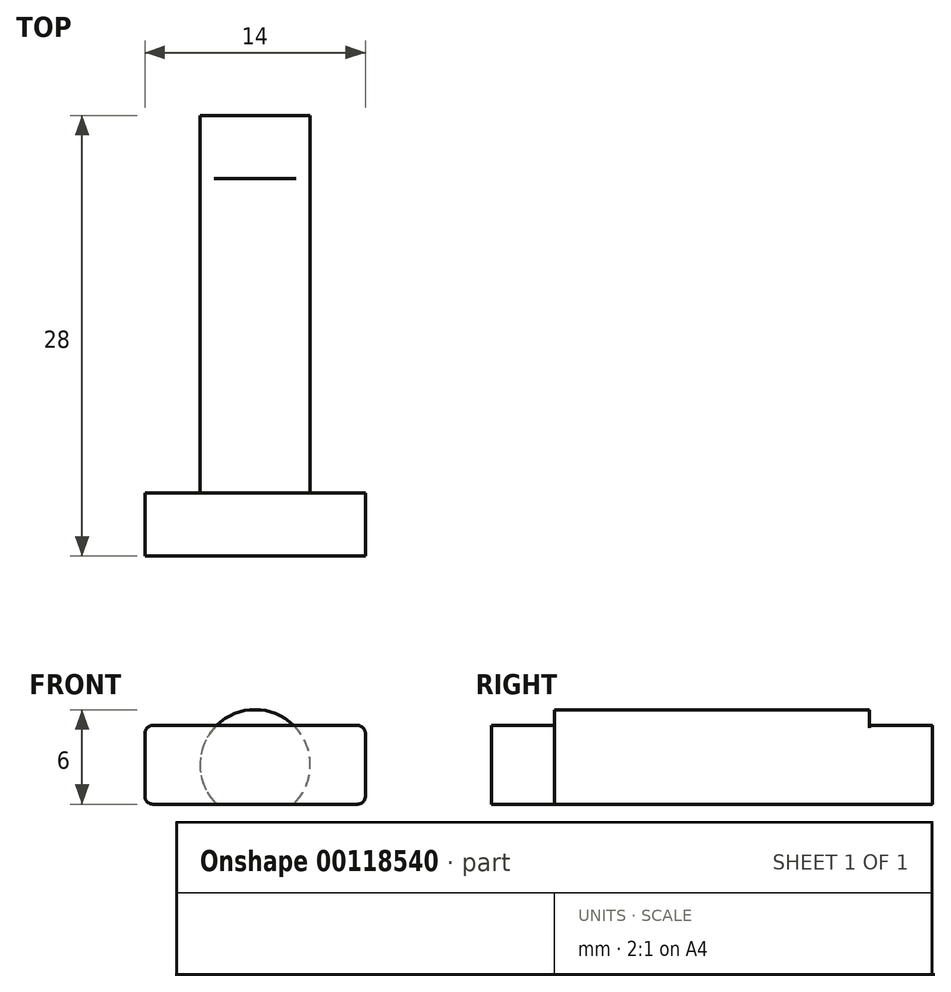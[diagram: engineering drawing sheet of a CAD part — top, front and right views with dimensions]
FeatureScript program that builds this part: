
annotation { "Feature Type Name" : "Feature", "Feature Type Description" : "" }
export const myFeature = defineFeature(function(context is Context, id is Id, definition is map)
    precondition{}
    {
        {
            var Q0;
            Q0=qCreatedBy(makeId("Front.planeOp"),FACE);
            var sketch = newSketch(context, id + "F0", { "sketchPlane" : qUnion([Q0])});
            skArc(sketch, "E0", {"start": v(2.45, 0) * mm, "mid": v(0, 6) * mm, "end": v(-2.45, 0) * mm});
            skLineSegment(sketch, "E1", {"start": v(-2.45, 0) * mm, "end": v(2.45, 0) * mm});
            skSolve(sketch);
        }
        {
            var Q0;
            Q0=makeQuery(id+"F0.imprint","IMPRINT",FACE,{"disambiguationData":[TD([[makeQuery(id+"F0.imprint","IMPRINT",EDGE,{"derivedFrom":sQuery(id+"F0.wireOp",EDGE,"E0")}),1.0]])]});
            extrude(context, id + "F1", {"entities" : qUnion([Q0]), "endBound" : BoundingType.SYMMETRIC, "depth" : 20 * mm});
        }
        {
            var Q0;
            Q0=makeQuery(id+"F1.opExtrude","CAP_FACE",FACE,{"disambiguationData":[OSD([sQuery(id+"F0.wireOp",EDGE,"E0"),sQuery(id+"F0.wireOp",EDGE,"E1")])],"isStart":false});
            var sketch = newSketch(context, id + "F2", { "sketchPlane" : qUnion([Q0])});
            skCircle(sketch, "E2", {"center": v(0, 2.5) * mm, "radius": 3.5 * mm, "construction": true});
            skLineSegment(sketch, "E3.bottom", {"start": v(-7, 5) * mm, "end": v(7, 5) * mm});
            skLineSegment(sketch, "E3.top", {"start": v(-7, 0) * mm, "end": v(7, 0) * mm});
            skLineSegment(sketch, "E3.left", {"start": v(-7, 5) * mm, "end": v(-7, 0) * mm});
            skLineSegment(sketch, "E3.right", {"start": v(7, 5) * mm, "end": v(7, 0) * mm});
            skSolve(sketch);
        }
        {
            var Q0;
            Q0=makeQuery(id+"F2.imprint","IMPRINT",FACE,{"disambiguationData":[TD([[makeQuery(id+"F2.imprint","IMPRINT",EDGE,{"derivedFrom":sQuery(id+"F2.wireOp",EDGE,"E3.bottom")}),-1.0]])]});
            extrude(context, id + "F3", {"entities" : qUnion([Q0]), "operationType" : NewBodyOperationType.ADD, "depth" : 4 * mm});
        }
        {
            var Q0;
            Q0=makeQuery(id+"F1.opExtrude","CAP_FACE",FACE,{"disambiguationData":[OSD([sQuery(id+"F0.wireOp",EDGE,"E0"),sQuery(id+"F0.wireOp",EDGE,"E1")])],"isStart":true});
            var sketch = newSketch(context, id + "F4", { "sketchPlane" : qUnion([Q0])});
            skCircle(sketch, "E4", {"center": v(0, 2.5) * mm, "radius": 3.5 * mm, "construction": true});
            skLineSegment(sketch, "E5.bottom", {"start": v(-2.45, 0) * mm, "end": v(2.45, 0) * mm});
            skLineSegment(sketch, "E5.top", {"start": v(-2.45, 5) * mm, "end": v(2.45, 5) * mm});
            skSolve(sketch);
        }
        {
            var Q0;
            Q0=makeQuery(id+"F4.imprint","IMPRINT",FACE,{"disambiguationData":[TD([[makeQuery(id+"F4.imprint","IMPRINT",EDGE,{"derivedFrom":sQuery(id+"F4.wireOp",EDGE,"E5.bottom")}),-1.0]])]});
            extrude(context, id + "F5", {"entities" : qUnion([Q0]), "operationType" : NewBodyOperationType.ADD, "depth" : 4 * mm});
        }
        {
            var Q0;
            Q0=makeQuery(id+"F3.opExtrude","SWEPT_EDGE",EDGE,{"disambiguationData":[OSD([sQuery(id+"F0.wireOp",EDGE,"E0"),sQuery(id+"F2.wireOp",EDGE,"E3.bottom"),sQuery(id+"F2.wireOp",EDGE,"E3.right")])]});
            var Q1;
            Q1=makeQuery(id+"F3.opExtrude","SWEPT_EDGE",EDGE,{"disambiguationData":[OSD([sQuery(id+"F0.wireOp",EDGE,"E0"),sQuery(id+"F2.wireOp",EDGE,"E3.top"),sQuery(id+"F2.wireOp",EDGE,"E3.right")])]});
            var Q2;
            Q2=makeQuery(id+"F3.opExtrude","SWEPT_EDGE",EDGE,{"disambiguationData":[OSD([sQuery(id+"F0.wireOp",EDGE,"E0"),sQuery(id+"F2.wireOp",EDGE,"E3.bottom"),sQuery(id+"F2.wireOp",EDGE,"E3.left")])]});
            var Q3;
            Q3=makeQuery(id+"F3.opExtrude","SWEPT_EDGE",EDGE,{"disambiguationData":[OSD([sQuery(id+"F0.wireOp",EDGE,"E0"),sQuery(id+"F2.wireOp",EDGE,"E3.top"),sQuery(id+"F2.wireOp",EDGE,"E3.left")])]});
            fillet(context, id + "F6", {"entities" : qUnion([Q0, Q1, Q2, Q3]), "radius" : .5 * mm, "tangentPropagation" : true, "allowEdgeOverflow" : false});
        }
        {
            var Q0;
            Q0=makeQuery(id+"F5.opExtrude","SWEPT_EDGE",EDGE,{"disambiguationData":[OSD([sQuery(id+"F0.wireOp",EDGE,"E0"),sQuery(id+"F4.wireOp",EDGE,"E5.top"),sQuery(id+"F4.wireOp",EDGE,"E5.right")])]});
            var Q1;
            Q1=makeQuery(id+"F5.opExtrude","SWEPT_EDGE",EDGE,{"disambiguationData":[OSD([sQuery(id+"F0.wireOp",EDGE,"E0"),sQuery(id+"F4.wireOp",EDGE,"E5.bottom"),sQuery(id+"F4.wireOp",EDGE,"E5.right")])]});
            var Q2;
            Q2=makeQuery(id+"F5.opExtrude","SWEPT_EDGE",EDGE,{"disambiguationData":[OSD([sQuery(id+"F0.wireOp",EDGE,"E0"),sQuery(id+"F4.wireOp",EDGE,"E5.top"),sQuery(id+"F4.wireOp",EDGE,"E5.left")])]});
            var Q3;
            Q3=makeQuery(id+"F5.opExtrude","SWEPT_EDGE",EDGE,{"disambiguationData":[OSD([sQuery(id+"F0.wireOp",EDGE,"E0"),sQuery(id+"F4.wireOp",EDGE,"E5.bottom"),sQuery(id+"F4.wireOp",EDGE,"E5.left")])]});
            fillet(context, id + "F7", {"entities" : qUnion([Q0, Q1, Q2, Q3]), "radius" : .5 * mm, "tangentPropagation" : true, "allowEdgeOverflow" : false});
        }
    });
